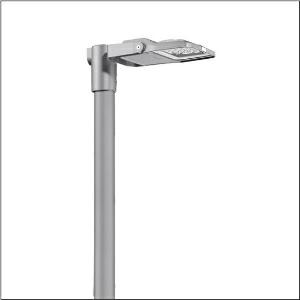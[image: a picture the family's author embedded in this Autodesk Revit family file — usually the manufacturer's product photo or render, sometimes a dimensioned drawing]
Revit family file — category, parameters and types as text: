
# Revit family: floodlight_fl_21_iq_micro___pl33t_5xa7762a4f3a_b73c
name_source: partatom
category: Lighting Fixtures
units: mm (PartAtom-declared; Revit-internal decimal feet)

## family parameters
Cut with Voids When Loaded = No
Host = Face
Light Source = No
Part Type = Normal
Room Calculation Point = No
Round Connector Dimension = Use Diameter
Shared = No

## types (1)
- --- (1 x LED, 3050 lm, 23.1 W, 4000K)
    Apparent Load = 23 VA
    CIE Flux Codes = 26 75 99 100 100
    Color Rendering = 70
    Color Temperature = 4000K
    Default Elevation = 1800 mm
    Description = Floodlight FL 21 iQ micro, floodlight, primary light control with lens, of PMMA, primary optical cover: protective disc, of toughened safety glass, transparent, light distribution: PL33T, light emission: direct distribution, installation type: surface-mounted, LED, High Power LED, rated luminous flux: 3.050lm, luminous efficacy: 132lm/W, light colour: 740, colour temperature: 4000K, control: Auto-Match, Temp-Guard, Night-Set, Smart-Wire, Desk-Remote (wireless, voltage-free reading and setting of iQ features in the workshop via application-optimized NFC function/RFID function), optimised constant luminous flux control (CLO 2.0), Street-Remote, with terminal, 6-pole, mains connection: 220..240V, AC, 50/60Hz, start of lifetime: 23W, end of service life: 24W, reduction: 11W, luminaire housing, of diecast aluminium, powder-coated, Siteco® metallic grey (DB 702S), corrosivity category C5 mid according to DIN EN ISO 12944, sealing non-destructively replaceable, please order mast flange separately, mast bracket, of steel, galvanised, powder-coated, Siteco® metallic grey (DB 702S), protection rating (complete): IP66, insulation class (complete): insulation class II (safety insulation), certification: CE, ENEC, VDE, protection symbol: D, impact resistance: IK07, permissible operating ambient temperature: -40..+40°C, permissible operating ambient temperature for outdoor applications: -40..+50°C, standard: DIN EN 12944, LABS conformity tested according to VDMA 24364:2018-05, packaging unit: 1 piece

Light Distribution: PL33T
    Height = 65 mm
    Lamp = 1 x LED
    Lamp Light Flux = 3050 lm
    Lamp Power = 23.1 W
    Lamp count = 1
    Length = 312 mm
    Luminous efficacy = 132 lm/W
    Manufacturer = Siteco
    ModVariant = No
    Model = 5XA7762A4F3A
    Number of Poles = 1
    OnlyDefault = Yes
    Power Factor = 1
    Product Name = Floodlight FL 21 iQ micro | PL33T
    Product group = floodlight | pylon annexe
    ProductGroupID = 6200
    Protection Class = Protection class II
    Protection Degree = IP 66
    RLX_Detail_Level = 1
    RLX_Emergency_Light_Flux = 0 lm
    RLX_Emergency_Type = 0
    RLX_Emergency_Type_DB = No
    RlxData = <blob elided: 101665 chars, md5=fedc78c1>
    Socket = socket
    Standby Power = 0 W
    System Light Flux = 3050 lm
    System Power = 23 W
    Type Comments = factory setting: luminous flux: 100 % | dim-lin: 254 | 455 mA
    Type Image = l_1007121.jpg
    URL = http://relux.com
    VarID = @adj_098023
    Voltage = 0 V
    Weight = 0.00 kg
    Width = 230 mm

## geometry (parser evidence)
native form markers: Blend x4, Sweep x10
no freeform markers — native parametric forms only
